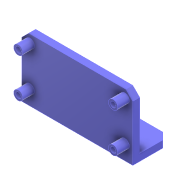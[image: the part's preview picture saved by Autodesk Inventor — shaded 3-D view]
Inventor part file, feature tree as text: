
AUTODESK INVENTOR PART (.ipt)
format: ipt  version: 2022 (Build 260153000, 153)  size: 195,072 bytes
history: native  units: mm
features: sketch x5, extrude x3, hole x2, chamfer x2, projected_geometry x2, rib x1
ambient origin geometry x8: Origin, YZ Plane, XZ Plane, XY Plane, X Axis, Y Axis, Z Axis, Center Point
bodies: Solid1 (feature_tree)
feature tree (15):
  extrude  "Extrusion1"  Depth=44.0mm
  extrude  "Extrusion2"  Depth=3.0mm TaperAngle=0.0deg
  hole  "Hole1"  [1 undecoded]
  rib  "Rib1"
  chamfer  "Chamfer1"  Distance=2.0mm
  hole  "Hole2"  [1 undecoded]
  chamfer  "Chamfer2"  Distance=10.0mm
  extrude  "Extrusion3"  Depth=5.0mm
  sketch  "Sketch1"  dims[d0=20.0mm d1=44.0mm]
  sketch  "Sketch2"  dims[d2=2.0mm d3=3.0mm d4=0.0mm]
  sketch  "Sketch3"  dims[d5=16.0mm d6=3.0mm d7=0.0mm]
  sketch  "Sketch5"  dims[d8=2.0mm]
  sketch  "Sketch6"  dims[d9=2.0mm d10=2.0mm d11=2.0mm d14=2.4mm d15=6.0mm d16=4.0mm d17=2.0mm d18=90.0deg d19=6.0mm d20=0.0mm d21=10.0mm d22=15.0mm d23=1.0mm d24=5.0mm d25=0.0mm d26=0.0mm d27=1.0mm d28=1.0mm d29=2.0mm d30=2.0mm d31=45.0deg d32=30.0mm d33=3.4mm d34=6.0mm d35=4.0mm d36=2.0mm d37=90.0deg d38=6.0mm d39=0.0mm d40=3.0mm d41=2.0mm d42=45.0deg d43=0.5mm d44=44.0mm d45=20.0mm d46=4.0mm d47=4.0mm d49=4.0mm d50=4.0mm d51=5.0mm d52=0.0mm]
  projected_geometry  "Project Cut Edges1"
  projected_geometry  "Project Cut Edges2"
note: 2 required parameter values undecoded (feature->parameter linkage not recoverable at this tier; creation-order binding heuristic only, values carry confidence <= 0.55)
